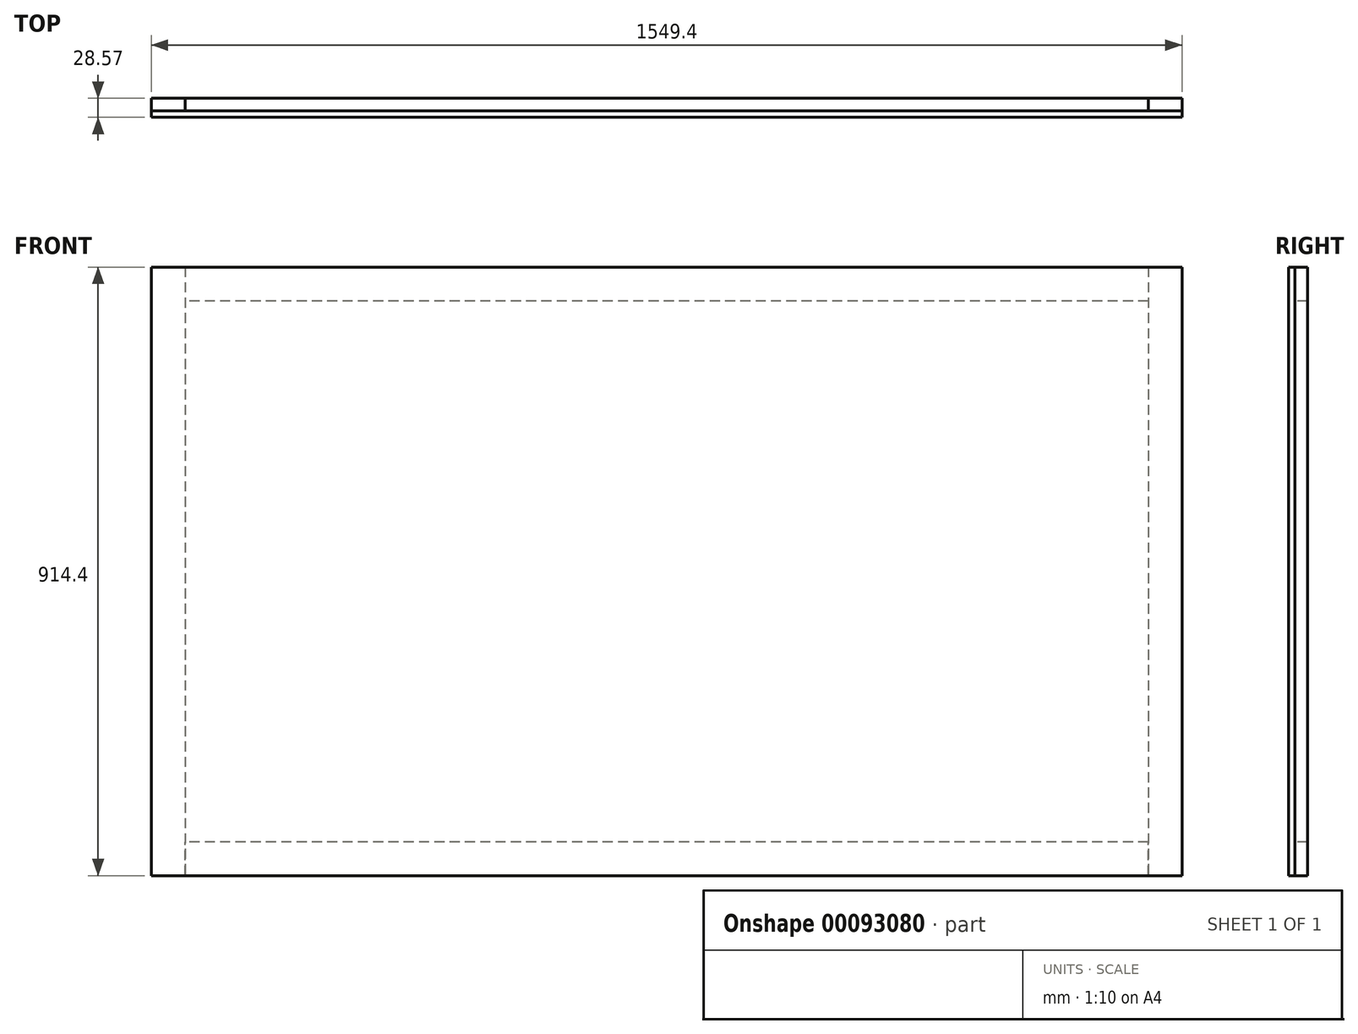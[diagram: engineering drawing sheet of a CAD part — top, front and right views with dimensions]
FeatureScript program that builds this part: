
annotation { "Feature Type Name" : "Feature", "Feature Type Description" : "" }
export const myFeature = defineFeature(function(context is Context, id is Id, definition is map)
    precondition{}
    {
        {
            var Q0;
            Q0=qCreatedBy(makeId("Front.planeOp"),FACE);
            var sketch = newSketch(context, id + "F0", { "sketchPlane" : qUnion([Q0])});
            skLineSegment(sketch, "E0.bottom", {"start": v(-774.7, 457.2) * mm, "end": v(774.7, 457.2) * mm});
            skLineSegment(sketch, "E0.top", {"start": v(-774.7, -457.2) * mm, "end": v(774.7, -457.2) * mm});
            skLineSegment(sketch, "E0.left", {"start": v(-774.7, 457.2) * mm, "end": v(-774.7, -457.2) * mm});
            skLineSegment(sketch, "E0.right", {"start": v(774.7, 457.2) * mm, "end": v(774.7, -457.2) * mm});
            skPoint(sketch, "E0.middle", {"position": v(0, 0) * mm});
            skSolve(sketch);
        }
        {
            var Q0;
            Q0 = qSketchRegion(id + "F0", true);
            extrude(context, id + "F1", {"entities" : qUnion([Q0]), "endBound" : BoundingType.SYMMETRIC, "depth" : 9.52 * mm});
        }
        {
            var Q0;
            Q0=makeQuery(id+"F1.opExtrude","CAP_FACE",FACE,{"disambiguationData":[OSD([sQuery(id+"F0.wireOp",EDGE,"E0.bottom"),sQuery(id+"F0.wireOp",EDGE,"E0.top"),sQuery(id+"F0.wireOp",EDGE,"E0.left"),sQuery(id+"F0.wireOp",EDGE,"E0.right")])],"isStart":true});
            var sketch = newSketch(context, id + "F2", { "sketchPlane" : qUnion([Q0])});
            skLineSegment(sketch, "E1.bottom", {"start": v(-774.7, 457.2) * mm, "end": v(-723.9, 457.2) * mm});
            skLineSegment(sketch, "E1.top", {"start": v(-774.7, -457.2) * mm, "end": v(-723.9, -457.2) * mm});
            skLineSegment(sketch, "E1.left", {"start": v(-774.7, 457.2) * mm, "end": v(-774.7, -457.2) * mm});
            skLineSegment(sketch, "E1.right", {"start": v(-723.9, 457.2) * mm, "end": v(-723.9, -457.2) * mm});
            skLineSegment(sketch, "E2.bottom", {"start": v(774.7, 457.2) * mm, "end": v(723.9, 457.2) * mm});
            skLineSegment(sketch, "E2.top", {"start": v(774.7, -457.2) * mm, "end": v(723.9, -457.2) * mm});
            skLineSegment(sketch, "E2.left", {"start": v(774.7, 457.2) * mm, "end": v(774.7, -457.2) * mm});
            skLineSegment(sketch, "E2.right", {"start": v(723.9, 457.2) * mm, "end": v(723.9, -457.2) * mm});
            skSolve(sketch);
        }
        {
            var Q0;
            Q0 = qSketchRegion(id + "F2", true);
            extrude(context, id + "F3", {"entities" : qUnion([Q0]), "depth" : 19.05 * mm});
        }
        {
            var Q0;
            Q0=makeQuery(id+"F1.opExtrude","CAP_FACE",FACE,{"disambiguationData":[OSD([sQuery(id+"F0.wireOp",EDGE,"E0.bottom"),sQuery(id+"F0.wireOp",EDGE,"E0.top"),sQuery(id+"F0.wireOp",EDGE,"E0.left"),sQuery(id+"F0.wireOp",EDGE,"E0.right")])],"isStart":true});
            var sketch = newSketch(context, id + "F4", { "sketchPlane" : qUnion([Q0])});
            skLineSegment(sketch, "E3.bottom", {"start": v(-723.9, 457.2) * mm, "end": v(723.9, 457.2) * mm});
            skLineSegment(sketch, "E3.top", {"start": v(-723.9, 406.4) * mm, "end": v(723.9, 406.4) * mm});
            skLineSegment(sketch, "E3.left", {"start": v(-723.9, 457.2) * mm, "end": v(-723.9, 406.4) * mm});
            skLineSegment(sketch, "E3.right", {"start": v(723.9, 457.2) * mm, "end": v(723.9, 406.4) * mm});
            skLineSegment(sketch, "E4.bottom", {"start": v(-723.9, -457.2) * mm, "end": v(723.9, -457.2) * mm});
            skLineSegment(sketch, "E4.top", {"start": v(-723.9, -406.4) * mm, "end": v(723.9, -406.4) * mm});
            skLineSegment(sketch, "E4.left", {"start": v(-723.9, -457.2) * mm, "end": v(-723.9, -406.4) * mm});
            skLineSegment(sketch, "E4.right", {"start": v(723.9, -457.2) * mm, "end": v(723.9, -406.4) * mm});
            skSolve(sketch);
        }
        {
            var Q0;
            Q0 = qSketchRegion(id + "F4", true);
            extrude(context, id + "F5", {"entities" : qUnion([Q0]), "depth" : 19.05 * mm});
        }
    });
